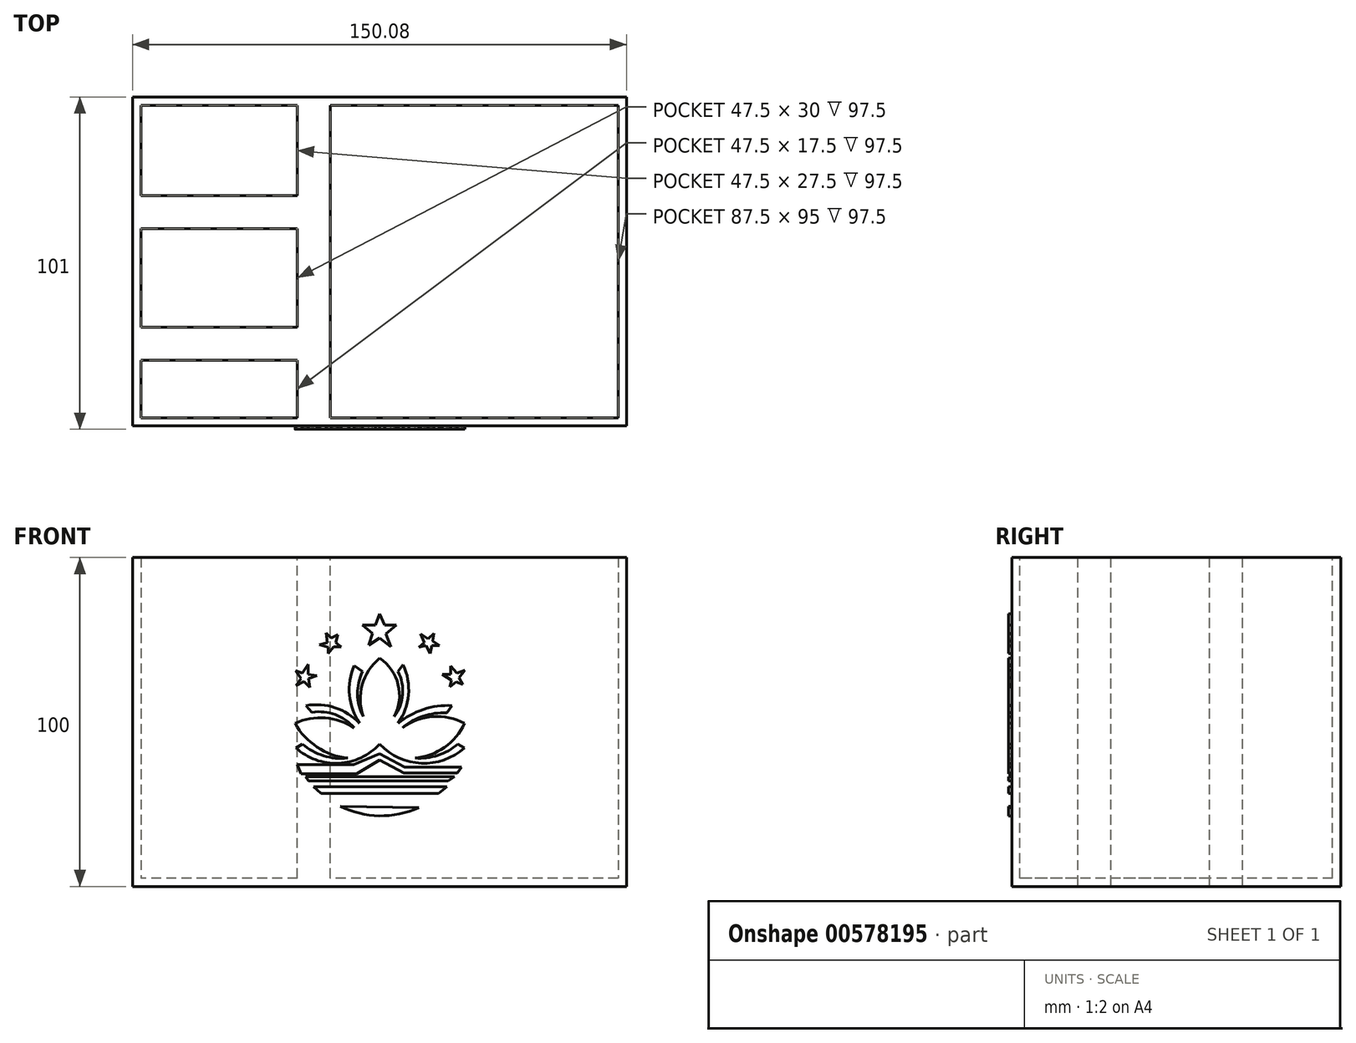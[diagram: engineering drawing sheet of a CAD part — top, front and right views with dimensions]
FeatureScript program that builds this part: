
annotation { "Feature Type Name" : "Feature", "Feature Type Description" : "" }
export const myFeature = defineFeature(function(context is Context, id is Id, definition is map)
    precondition{}
    {
        {
            var Q0;
            Q0=qCreatedBy(makeId("Top.planeOp"),FACE);
            var sketch = newSketch(context, id + "F0", { "sketchPlane" : qUnion([Q0])});
            skLineSegment(sketch, "E0.bottom", {"start": v(75, 50) * mm, "end": v(-75, 50) * mm});
            skLineSegment(sketch, "E0.top", {"start": v(75, -50) * mm, "end": v(-75, -50) * mm});
            skLineSegment(sketch, "E0.left", {"start": v(75, 50) * mm, "end": v(75, -50) * mm});
            skLineSegment(sketch, "E0.right", {"start": v(-75, 50) * mm, "end": v(-75, -50) * mm});
            skPoint(sketch, "E0.middle", {"position": v(0, 0) * mm});
            skSolve(sketch);
        }
        {
            var Q0;
            Q0=makeQuery(id+"F0.imprint","IMPRINT",FACE,{"disambiguationData":[TD([[makeQuery(id+"F0.imprint","IMPRINT",EDGE,{"derivedFrom":sQuery(id+"F0.wireOp",EDGE,"E0.bottom")}),1.0]])]});
            extrude(context, id + "F1", {"entities" : qUnion([Q0]), "depth" : 100 * mm, "offsetDistance" : 25 * mm});
        }
        {
            var Q0;
            Q0=makeQuery(id+"F1.opExtrude","CAP_FACE",FACE,{"disambiguationData":[OSD([sQuery(id+"F0.wireOp",EDGE,"E0.bottom"),sQuery(id+"F0.wireOp",EDGE,"E0.top"),sQuery(id+"F0.wireOp",EDGE,"E0.left"),sQuery(id+"F0.wireOp",EDGE,"E0.right")])],"isStart":false});
            shell(context, id + "F2", {"entities" : qUnion([Q0]), "thickness" : 2.5 * mm});
        }
        {
            var Q0;
            Q0=qCreatedBy(makeId("Top.planeOp"),FACE);
            var sketch = newSketch(context, id + "F3", { "sketchPlane" : qUnion([Q0])});
            skLineSegment(sketch, "E1.bottom", {"start": v(-25, 50) * mm, "end": v(-15, 50) * mm});
            skLineSegment(sketch, "E1.top", {"start": v(-25, -50) * mm, "end": v(-15, -50) * mm});
            skLineSegment(sketch, "E1.left", {"start": v(-25, 50) * mm, "end": v(-25, -50) * mm});
            skLineSegment(sketch, "E1.right", {"start": v(-15, 50) * mm, "end": v(-15, -50) * mm});
            skPoint(sketch, "E2.oppositeSnap0", {"position": v(-25, 10) * mm});
            skLineSegment(sketch, "E2.bottom", {"start": v(-25, 20) * mm, "end": v(-75.08, 20) * mm});
            skLineSegment(sketch, "E2.top", {"start": v(-25, 10) * mm, "end": v(-75.08, 10) * mm});
            skLineSegment(sketch, "E2.left", {"start": v(-25, 20) * mm, "end": v(-25, 10) * mm});
            skLineSegment(sketch, "E2.right", {"start": v(-75.08, 20) * mm, "end": v(-75.08, 10) * mm});
            skLineSegment(sketch, "E3.bottom", {"start": v(-25, -20) * mm, "end": v(-75.08, -20) * mm});
            skLineSegment(sketch, "E3.top", {"start": v(-25, -30) * mm, "end": v(-75.08, -30) * mm});
            skLineSegment(sketch, "E3.left", {"start": v(-25, -20) * mm, "end": v(-25, -30) * mm});
            skLineSegment(sketch, "E3.right", {"start": v(-75.08, -20) * mm, "end": v(-75.08, -30) * mm});
            skSolve(sketch);
        }
        {
            var Q0;
            Q0 = qSketchRegion(id + "F3", true);
            extrude(context, id + "F4", {"entities" : qUnion([Q0]), "operationType" : NewBodyOperationType.ADD, "depth" : 100 * mm, "offsetDistance" : 25 * mm});
        }
        {
            var Q0;
            Q0=makeQuery(id+"F1.opExtrude","SWEPT_FACE",FACE,{"disambiguationData":[OSD([sQuery(id+"F0.wireOp",EDGE,"E0.top")])]});
            var sketch = newSketch(context, id + "F5", { "sketchPlane" : qUnion([Q0])});
            skLineSegment(sketch, "E4", {"start": v(0, 82.9) * mm, "end": v(-1.33, 79.44) * mm});
            skLineSegment(sketch, "E5", {"start": v(-1.33, 79.44) * mm, "end": v(-5.25, 79.44) * mm});
            skLineSegment(sketch, "E6", {"start": v(-5.25, 79.44) * mm, "end": v(-2.15, 76.97) * mm});
            skLineSegment(sketch, "E7", {"start": v(-2.15, 76.97) * mm, "end": v(-3.29, 73.35) * mm});
            skLineSegment(sketch, "E8", {"start": v(-3.29, 73.35) * mm, "end": v(0, 75.52) * mm});
            skLineSegment(sketch, "E9", {"start": v(0, 75.52) * mm, "end": v(3.42, 72.84) * mm});
            skLineSegment(sketch, "E10", {"start": v(3.42, 72.84) * mm, "end": v(1.87, 76.76) * mm});
            skLineSegment(sketch, "E11", {"start": v(1.87, 76.76) * mm, "end": v(5.07, 79.44) * mm});
            skLineSegment(sketch, "E12", {"start": v(5.07, 79.44) * mm, "end": v(1.46, 79.44) * mm});
            skLineSegment(sketch, "E13", {"start": v(1.46, 79.44) * mm, "end": v(0, 82.9) * mm});
            skLineSegment(sketch, "E14", {"start": v(16.52, 76.97) * mm, "end": v(14.76, 75.21) * mm});
            skLineSegment(sketch, "E15", {"start": v(14.76, 75.21) * mm, "end": v(12.5, 76.76) * mm});
            skLineSegment(sketch, "E16", {"start": v(12.5, 76.76) * mm, "end": v(13.63, 74.08) * mm});
            skLineSegment(sketch, "E17", {"start": v(13.63, 74.08) * mm, "end": v(11.98, 72.74) * mm});
            skLineSegment(sketch, "E18", {"start": v(11.98, 72.74) * mm, "end": v(14.15, 73.25) * mm});
            skLineSegment(sketch, "E19", {"start": v(14.15, 73.25) * mm, "end": v(15.38, 70.88) * mm});
            skLineSegment(sketch, "E20", {"start": v(15.38, 70.88) * mm, "end": v(15.9, 73.25) * mm});
            skLineSegment(sketch, "E21", {"start": v(15.9, 73.25) * mm, "end": v(18.17, 73.25) * mm});
            skLineSegment(sketch, "E22", {"start": v(18.17, 73.25) * mm, "end": v(16.1, 74.6) * mm});
            skLineSegment(sketch, "E23", {"start": v(21.57, 67.06) * mm, "end": v(21.57, 64.48) * mm});
            skLineSegment(sketch, "E24", {"start": v(21.57, 64.48) * mm, "end": v(19.1, 64.48) * mm});
            skLineSegment(sketch, "E25", {"start": v(19.1, 64.48) * mm, "end": v(21.78, 62.73) * mm});
            skLineSegment(sketch, "E26", {"start": v(21.78, 62.73) * mm, "end": v(21.26, 60.67) * mm});
            skLineSegment(sketch, "E27", {"start": v(21.26, 60.67) * mm, "end": v(23.22, 62.22) * mm});
            skLineSegment(sketch, "E28", {"start": v(23.22, 62.22) * mm, "end": v(25.29, 61.39) * mm});
            skLineSegment(sketch, "E29", {"start": v(25.29, 61.39) * mm, "end": v(24.15, 63.45) * mm});
            skLineSegment(sketch, "E30", {"start": v(24.15, 63.45) * mm, "end": v(25.9, 65.72) * mm});
            skLineSegment(sketch, "E31", {"start": v(25.9, 65.72) * mm, "end": v(23.43, 64.8) * mm});
            skLineSegment(sketch, "E32", {"start": v(23.43, 64.8) * mm, "end": v(21.57, 67.06) * mm});
            skLineSegment(sketch, "E33", {"start": v(-12.67, 76.55) * mm, "end": v(-14.74, 75.52) * mm});
            skLineSegment(sketch, "E34", {"start": v(-14.74, 75.52) * mm, "end": v(-16.28, 77.07) * mm});
            skLineSegment(sketch, "E35", {"start": v(-16.28, 77.07) * mm, "end": v(-15.87, 74.18) * mm});
            skLineSegment(sketch, "E36", {"start": v(-15.87, 74.18) * mm, "end": v(-18.24, 73.46) * mm});
            skLineSegment(sketch, "E37", {"start": v(-18.24, 73.46) * mm, "end": v(-15.66, 72.74) * mm});
            skLineSegment(sketch, "E38", {"start": v(-15.66, 72.74) * mm, "end": v(-15.66, 70.88) * mm});
            skLineSegment(sketch, "E39", {"start": v(-15.66, 70.88) * mm, "end": v(-14.01, 72.84) * mm});
            skLineSegment(sketch, "E40", {"start": v(-14.01, 72.84) * mm, "end": v(-11.74, 72.84) * mm});
            skLineSegment(sketch, "E41", {"start": v(-11.74, 72.84) * mm, "end": v(-13.3, 74.18) * mm});
            skLineSegment(sketch, "E42", {"start": v(-13.3, 74.18) * mm, "end": v(-12.67, 76.55) * mm});
            skLineSegment(sketch, "E43", {"start": v(16.1, 74.6) * mm, "end": v(16.52, 76.97) * mm});
            skLineSegment(sketch, "E44", {"start": v(-21.75, 67.48) * mm, "end": v(-23.45, 64.86) * mm});
            skLineSegment(sketch, "E45", {"start": v(-23.45, 64.86) * mm, "end": v(-25.57, 65.62) * mm});
            skLineSegment(sketch, "E46", {"start": v(-25.57, 65.62) * mm, "end": v(-23.92, 63.14) * mm});
            skLineSegment(sketch, "E47", {"start": v(-23.92, 63.14) * mm, "end": v(-25.36, 60.98) * mm});
            skLineSegment(sketch, "E48", {"start": v(-25.36, 60.98) * mm, "end": v(-22.99, 62.32) * mm});
            skLineSegment(sketch, "E49", {"start": v(-22.99, 62.32) * mm, "end": v(-21.23, 60.56) * mm});
            skLineSegment(sketch, "E50", {"start": v(-21.23, 60.56) * mm, "end": v(-21.61, 63.22) * mm});
            skLineSegment(sketch, "E51", {"start": v(-21.61, 63.22) * mm, "end": v(-19.07, 64.07) * mm});
            skArc(sketch, "E52", {"start": v(25.82, 49.6) * mm, "mid": v(16.18, 51.62) * mm, "end": v(6.93, 48.24) * mm});
            skArc(sketch, "E53", {"start": v(10.75, 39.02) * mm, "mid": v(19.7, 42.28) * mm, "end": v(25.82, 49.6) * mm});
            skArc(sketch, "E54", {"start": v(10.75, 39.02) * mm, "mid": v(17.7, 39.88) * mm, "end": v(23.8, 43.3) * mm});
            skArc(sketch, "E55", {"start": v(0, 43.3) * mm, "mid": v(12.68, 37.45) * mm, "end": v(25.82, 42.17) * mm});
            skArc(sketch, "E56", {"start": v(-25.47, 42.17) * mm, "mid": v(-12.5, 37.45) * mm, "end": v(0, 43.3) * mm});
            skArc(sketch, "E57", {"start": v(-23.45, 43.3) * mm, "mid": v(-17.03, 39.73) * mm, "end": v(-9.72, 39.02) * mm});
            skArc(sketch, "E58", {"start": v(-25.7, 49.6) * mm, "mid": v(-19, 42.36) * mm, "end": v(-9.72, 39.02) * mm});
            skArc(sketch, "E59", {"start": v(-7.7, 48.24) * mm, "mid": v(-16.52, 51.2) * mm, "end": v(-25.7, 49.6) * mm});
            skArc(sketch, "E60", {"start": v(-7.7, 48.24) * mm, "mid": v(-13.51, 52.23) * mm, "end": v(-20.52, 52.97) * mm});
            skArc(sketch, "E61", {"start": v(-6.12, 49.6) * mm, "mid": v(-13.54, 54.33) * mm, "end": v(-22.32, 54.99) * mm});
            skArc(sketch, "E62", {"start": v(-7.7, 67.14) * mm, "mid": v(-9.15, 58.16) * mm, "end": v(-6.12, 49.6) * mm});
            skArc(sketch, "E63", {"start": v(-5.22, 65.34) * mm, "mid": v(-6.72, 58.45) * mm, "end": v(-5, 51.62) * mm});
            skArc(sketch, "E64", {"start": v(0, 69.39) * mm, "mid": v(-5.29, 61.29) * mm, "end": v(-5, 51.62) * mm});
            skArc(sketch, "E65", {"start": v(4.45, 51.62) * mm, "mid": v(5.62, 61.35) * mm, "end": v(0, 69.39) * mm});
            skArc(sketch, "E66", {"start": v(4.45, 51.62) * mm, "mid": v(7, 58.31) * mm, "end": v(5.58, 65.34) * mm});
            skArc(sketch, "E67", {"start": v(5.58, 49.6) * mm, "mid": v(8.76, 58.26) * mm, "end": v(7.15, 67.36) * mm});
            skArc(sketch, "E68", {"start": v(22, 54.99) * mm, "mid": v(13.29, 53.81) * mm, "end": v(5.58, 49.6) * mm});
            skLineSegment(sketch, "E69", {"start": v(-7.7, 67.14) * mm, "end": v(-5.22, 65.34) * mm});
            skLineSegment(sketch, "E70", {"start": v(7.15, 67.36) * mm, "end": v(5.58, 65.34) * mm});
            skLineSegment(sketch, "E71", {"start": v(-22.32, 54.99) * mm, "end": v(-20.52, 52.97) * mm});
            skLineSegment(sketch, "E72", {"start": v(-23.45, 43.3) * mm, "end": v(-25.47, 42.17) * mm});
            skLineSegment(sketch, "E73", {"start": v(23.8, 43.3) * mm, "end": v(25.82, 42.17) * mm});
            skArc(sketch, "E74", {"start": v(20.42, 52.74) * mm, "mid": v(13.24, 51.78) * mm, "end": v(6.93, 48.24) * mm});
            skLineSegment(sketch, "E75", {"start": v(22, 54.99) * mm, "end": v(20.42, 52.74) * mm});
            skLineSegment(sketch, "E76", {"start": v(-20.07, 30.24) * mm, "end": v(20.42, 30.24) * mm});
            skLineSegment(sketch, "E77", {"start": v(20.42, 30.24) * mm, "end": v(17.95, 28.22) * mm});
            skLineSegment(sketch, "E78", {"start": v(17.95, 28.22) * mm, "end": v(-17.82, 28.22) * mm});
            skLineSegment(sketch, "E79", {"start": v(-17.82, 28.22) * mm, "end": v(-20.07, 30.24) * mm});
            skLineSegment(sketch, "E80", {"start": v(-16.7, 27.1) * mm, "end": v(-14, 25.28) * mm});
            skLineSegment(sketch, "E81", {"start": v(-14, 25.28) * mm, "end": v(14.12, 25.28) * mm});
            skArc(sketch, "E82", {"start": v(-11.97, 24.4) * mm, "mid": v(-0.1, 21.47) * mm, "end": v(11.87, 23.94) * mm});
            skLineSegment(sketch, "E83", {"start": v(-11.97, 24.4) * mm, "end": v(11.87, 23.94) * mm});
            skLineSegment(sketch, "E84", {"start": v(-22.55, 33.4) * mm, "end": v(22.67, 33.4) * mm});
            skLineSegment(sketch, "E85", {"start": v(22.67, 33.4) * mm, "end": v(20.82, 32.04) * mm});
            skLineSegment(sketch, "E86", {"start": v(20.82, 32.04) * mm, "end": v(-21.65, 32.04) * mm});
            skLineSegment(sketch, "E87", {"start": v(-21.65, 32.04) * mm, "end": v(-22.55, 33.4) * mm});
            skLineSegment(sketch, "E88", {"start": v(-25.02, 37) * mm, "end": v(-7.92, 37) * mm});
            skLineSegment(sketch, "E89", {"start": v(-7.92, 37) * mm, "end": v(0, 40.3) * mm});
            skLineSegment(sketch, "E90", {"start": v(0, 40.3) * mm, "end": v(7.6, 36.32) * mm});
            skLineSegment(sketch, "E91", {"start": v(7.6, 36.32) * mm, "end": v(24.92, 36.32) * mm});
            skLineSegment(sketch, "E92", {"start": v(24.92, 36.32) * mm, "end": v(23.57, 34.52) * mm});
            skLineSegment(sketch, "E93", {"start": v(23.57, 34.52) * mm, "end": v(7.38, 34.52) * mm});
            skLineSegment(sketch, "E94", {"start": v(7.38, 34.52) * mm, "end": v(0, 38.37) * mm});
            skLineSegment(sketch, "E95", {"start": v(0, 38.37) * mm, "end": v(-7.02, 34.3) * mm});
            skLineSegment(sketch, "E96", {"start": v(-7.02, 34.3) * mm, "end": v(-23.9, 34.3) * mm});
            skLineSegment(sketch, "E97", {"start": v(-23.9, 34.3) * mm, "end": v(-25.02, 37) * mm});
            skLineSegment(sketch, "E98", {"start": v(-21.75, 67.48) * mm, "end": v(-21.75, 64.48) * mm});
            skLineSegment(sketch, "E99", {"start": v(-21.75, 64.48) * mm, "end": v(-19.07, 64.07) * mm});
            skSolve(sketch);
        }
        {
            var Q0;
            Q0 = qSketchRegion(id + "F5", true);
            extrude(context, id + "F6", {"entities" : qUnion([Q0]), "operationType" : NewBodyOperationType.ADD, "depth" : 1 * mm, "offsetDistance" : 25 * mm});
        }
    });
